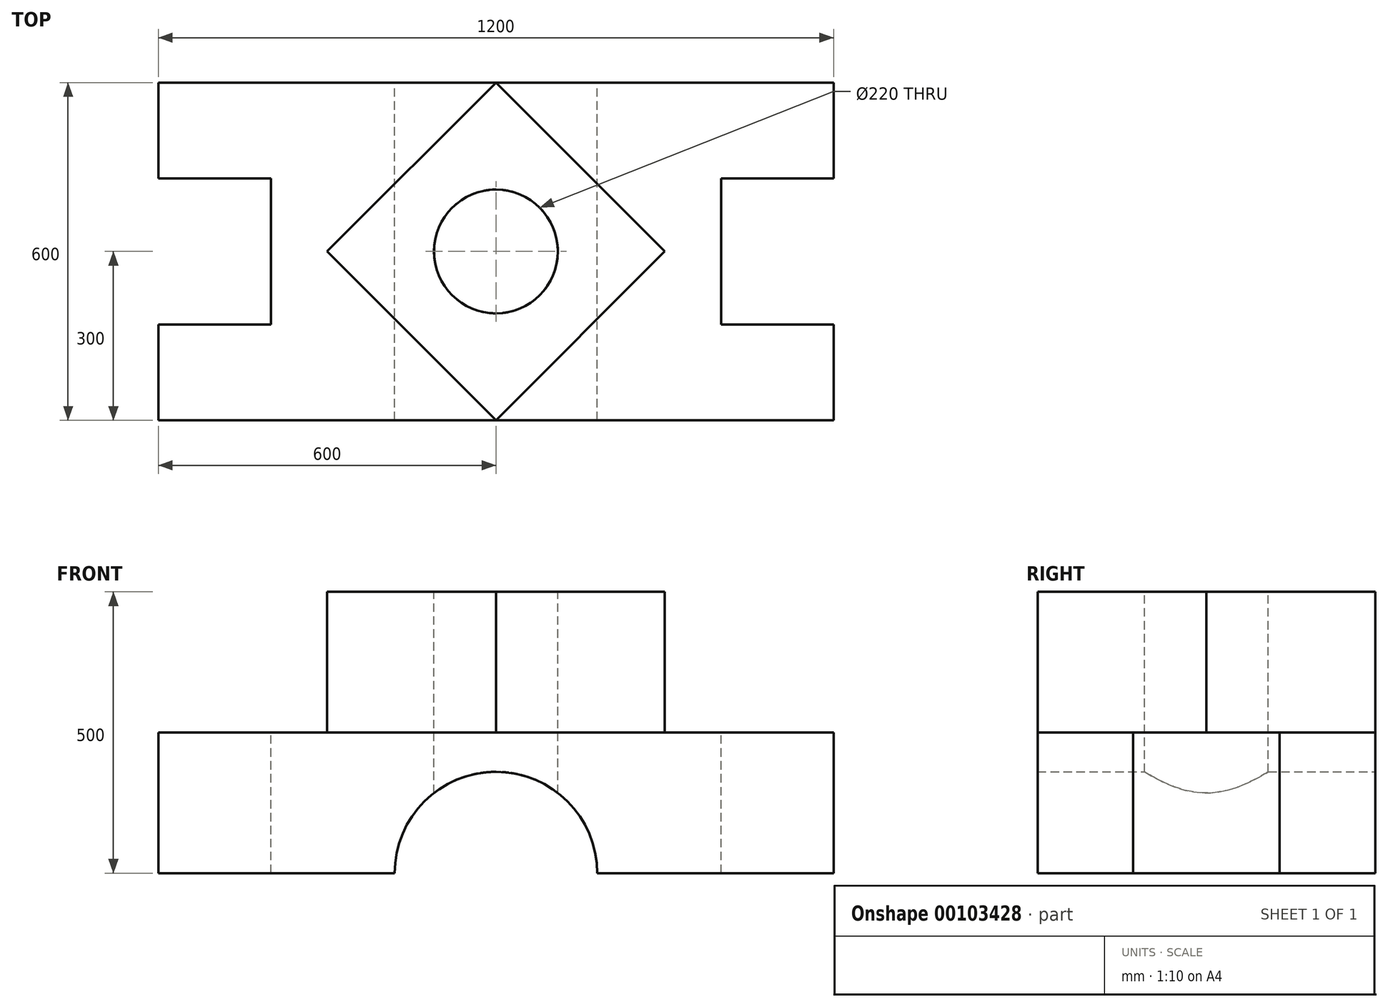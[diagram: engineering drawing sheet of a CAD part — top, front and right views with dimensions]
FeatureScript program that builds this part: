
annotation { "Feature Type Name" : "Feature", "Feature Type Description" : "" }
export const myFeature = defineFeature(function(context is Context, id is Id, definition is map)
    precondition{}
    {
        {
            var Q0;
            Q0=qCreatedBy(makeId("Front.planeOp"),FACE);
            var sketch = newSketch(context, id + "F0", { "sketchPlane" : qUnion([Q0])});
            skLineSegment(sketch, "E0.bottom", {"start": v(-600, -125) * mm, "end": v(-180, -125) * mm});
            skLineSegment(sketch, "E0.top", {"start": v(-600, 125) * mm, "end": v(-300, 125) * mm});
            skLineSegment(sketch, "E0.left", {"start": v(-600, -125) * mm, "end": v(-600, 125) * mm});
            skLineSegment(sketch, "E0.right", {"start": v(600, -125) * mm, "end": v(600, 125) * mm});
            skPoint(sketch, "E0.middle", {"position": v(0, 0) * mm});
            skLineSegment(sketch, "E1.bottom", {"start": v(300, 375) * mm, "end": v(-300, 375) * mm});
            skLineSegment(sketch, "E1.left", {"start": v(300, 375) * mm, "end": v(300, 125) * mm});
            skLineSegment(sketch, "E1.right", {"start": v(-300, 375) * mm, "end": v(-300, 125) * mm});
            skPoint(sketch, "E1.middle", {"position": v(0, 125) * mm});
            skPoint(sketch, "E2.orphan", {"position": v(-300, -125) * mm});
            skLineSegment(sketch, "E3.trimOffspring", {"start": v(300, 125) * mm, "end": v(600, 125) * mm});
            skPoint(sketch, "E4.orphan", {"position": v(300, -125) * mm});
            skArc(sketch, "E5", {"start": v(180, -125) * mm, "mid": v(0, 55) * mm, "end": v(-180, -125) * mm});
            skLineSegment(sketch, "E6.trimOffspring", {"start": v(180, -125) * mm, "end": v(600, -125) * mm});
            skSolve(sketch);
        }
        {
            var Q0;
            Q0 = qSketchRegion(id + "F0", true);
            extrude(context, id + "F1", {"entities" : qUnion([Q0]), "depth" : 600 * mm});
        }
        {
            var Q0;
            Q0=makeQuery(id+"F1.opExtrude","SWEPT_FACE",FACE,{"disambiguationData":[OSD([sQuery(id+"F0.wireOp",EDGE,"E3.trimOffspring")])]});
            var sketch = newSketch(context, id + "F2", { "sketchPlane" : qUnion([Q0])});
            skLineSegment(sketch, "E7.bottom", {"start": v(400, -170) * mm, "end": v(800, -170) * mm});
            skLineSegment(sketch, "E7.top", {"start": v(400, -430) * mm, "end": v(800, -430) * mm});
            skLineSegment(sketch, "E7.left", {"start": v(400, -170) * mm, "end": v(400, -430) * mm});
            skLineSegment(sketch, "E7.right", {"start": v(800, -170) * mm, "end": v(800, -430) * mm});
            skPoint(sketch, "E7.middle", {"position": v(600, -300) * mm});
            skSolve(sketch);
        }
        {
            var Q0;
            Q0 = qSketchRegion(id + "F2", true);
            extrude(context, id + "F3", {"entities" : qUnion([Q0]), "operationType" : NewBodyOperationType.REMOVE, "endBound" : BoundingType.THROUGH_ALL, "oppositeDirection" : true, "depth" : 25 * mm});
        }
        {
            var Q0;
            Q0=makeQuery(id+"F1.opExtrude","SWEPT_FACE",FACE,{"disambiguationData":[OSD([sQuery(id+"F0.wireOp",EDGE,"E0.top")])]});
            var sketch = newSketch(context, id + "F4", { "sketchPlane" : qUnion([Q0])});
            skLineSegment(sketch, "E8.bottom", {"start": v(-800, -170) * mm, "end": v(-400, -170) * mm});
            skLineSegment(sketch, "E8.top", {"start": v(-800, -430) * mm, "end": v(-400, -430) * mm});
            skLineSegment(sketch, "E8.left", {"start": v(-800, -170) * mm, "end": v(-800, -430) * mm});
            skLineSegment(sketch, "E8.right", {"start": v(-400, -170) * mm, "end": v(-400, -430) * mm});
            skPoint(sketch, "E8.middle", {"position": v(-600, -300) * mm});
            skSolve(sketch);
        }
        {
            var Q0;
            Q0 = qSketchRegion(id + "F2", true);
            extrude(context, id + "F5", {"entities" : qUnion([Q0]), "operationType" : NewBodyOperationType.REMOVE, "endBound" : BoundingType.THROUGH_ALL, "oppositeDirection" : true, "depth" : 25 * mm});
        }
        {
            var Q0;
            Q0 = qSketchRegion(id + "F4", true);
            extrude(context, id + "F6", {"entities" : qUnion([Q0]), "operationType" : NewBodyOperationType.REMOVE, "endBound" : BoundingType.THROUGH_ALL, "oppositeDirection" : true, "depth" : 25 * mm});
        }
        {
            var Q0;
            Q0=makeQuery(id+"F1.opExtrude","SWEPT_FACE",FACE,{"disambiguationData":[OSD([sQuery(id+"F0.wireOp",EDGE,"E1.bottom")])]});
            var sketch = newSketch(context, id + "F7", { "sketchPlane" : qUnion([Q0])});
            skLineSegment(sketch, "E9", {"start": v(0, -600) * mm, "end": v(-300, -300) * mm});
            skLineSegment(sketch, "E10", {"start": v(-300, -300) * mm, "end": v(0, 0) * mm});
            skLineSegment(sketch, "E11", {"start": v(0, 0) * mm, "end": v(300, -300) * mm});
            skLineSegment(sketch, "E12", {"start": v(300, -300) * mm, "end": v(0, -600) * mm});
            skLineSegment(sketch, "E13", {"start": v(300, -600) * mm, "end": v(0, -600) * mm});
            skLineSegment(sketch, "E14", {"start": v(300, -600) * mm, "end": v(300, -300) * mm});
            skSolve(sketch);
        }
        {
            var Q0;
            Q0=makeQuery(id+"F7.imprint","IMPRINT",FACE,{"disambiguationData":[TD([[makeQuery(id+"F7.imprint","IMPRINT",EDGE,{"derivedFrom":sQuery(id+"F7.wireOp",EDGE,"E12")}),1.0]])]});
            extrude(context, id + "F8", {"entities" : qUnion([Q0]), "operationType" : NewBodyOperationType.REMOVE, "oppositeDirection" : true, "depth" : 250 * mm});
        }
        {
            var Q0;
            Q0=makeQuery(id+"F1.opExtrude","SWEPT_FACE",FACE,{"disambiguationData":[OSD([sQuery(id+"F0.wireOp",EDGE,"E1.bottom")])]});
            var sketch = newSketch(context, id + "F9", { "sketchPlane" : qUnion([Q0])});
            skLineSegment(sketch, "E15", {"start": v(0, -600) * mm, "end": v(-300, -600) * mm});
            skLineSegment(sketch, "E16", {"start": v(-300, -600) * mm, "end": v(-300, -300) * mm});
            skLineSegment(sketch, "E17", {"start": v(-300, -300) * mm, "end": v(0, -600) * mm});
            skSolve(sketch);
        }
        {
            var Q0;
            Q0 = qSketchRegion(id + "F9", true);
            extrude(context, id + "F10", {"entities" : qUnion([Q0]), "operationType" : NewBodyOperationType.REMOVE, "oppositeDirection" : true, "depth" : 250 * mm});
        }
        {
            var Q0;
            Q0=makeQuery(id+"F1.opExtrude","SWEPT_FACE",FACE,{"disambiguationData":[OSD([sQuery(id+"F0.wireOp",EDGE,"E1.bottom")])]});
            var sketch = newSketch(context, id + "F11", { "sketchPlane" : qUnion([Q0])});
            skLineSegment(sketch, "E18", {"start": v(300, 0) * mm, "end": v(300, -300) * mm});
            skLineSegment(sketch, "E19", {"start": v(300, -300) * mm, "end": v(0, 0) * mm});
            skLineSegment(sketch, "E20", {"start": v(0, 0) * mm, "end": v(300, 0) * mm});
            skSolve(sketch);
        }
        {
            var Q0;
            Q0 = qSketchRegion(id + "F11", true);
            extrude(context, id + "F12", {"entities" : qUnion([Q0]), "operationType" : NewBodyOperationType.REMOVE, "oppositeDirection" : true, "depth" : 250 * mm});
        }
        {
            var Q0;
            Q0=makeQuery(id+"F1.opExtrude","SWEPT_FACE",FACE,{"disambiguationData":[OSD([sQuery(id+"F0.wireOp",EDGE,"E1.bottom")])]});
            var sketch = newSketch(context, id + "F13", { "sketchPlane" : qUnion([Q0])});
            skLineSegment(sketch, "E21", {"start": v(-300, 0) * mm, "end": v(0, 0) * mm});
            skLineSegment(sketch, "E22", {"start": v(0, 0) * mm, "end": v(-300, -300) * mm});
            skSolve(sketch);
        }
        {
            var Q0;
            Q0=makeQuery(id+"F13.imprint","IMPRINT",FACE,{"disambiguationData":[TD([[makeQuery(id+"F13.imprint","IMPRINT",EDGE,{"derivedFrom":sQuery(id+"F13.wireOp",EDGE,"E21")}),1.0]])]});
            extrude(context, id + "F14", {"entities" : qUnion([Q0]), "operationType" : NewBodyOperationType.REMOVE, "oppositeDirection" : true, "depth" : 250 * mm});
        }
        {
            var Q0;
            Q0=makeQuery(id+"F1.opExtrude","SWEPT_FACE",FACE,{"disambiguationData":[OSD([sQuery(id+"F0.wireOp",EDGE,"E1.bottom")])]});
            var sketch = newSketch(context, id + "F15", { "sketchPlane" : qUnion([Q0])});
            skCircle(sketch, "E23", {"center": v(0, -300) * mm, "radius": 110 * mm});
            skSolve(sketch);
        }
        {
            var Q0;
            Q0 = qSketchRegion(id + "F15", true);
            extrude(context, id + "F16", {"entities" : qUnion([Q0]), "operationType" : NewBodyOperationType.REMOVE, "endBound" : BoundingType.THROUGH_ALL, "oppositeDirection" : true, "depth" : 250 * mm});
        }
    });
